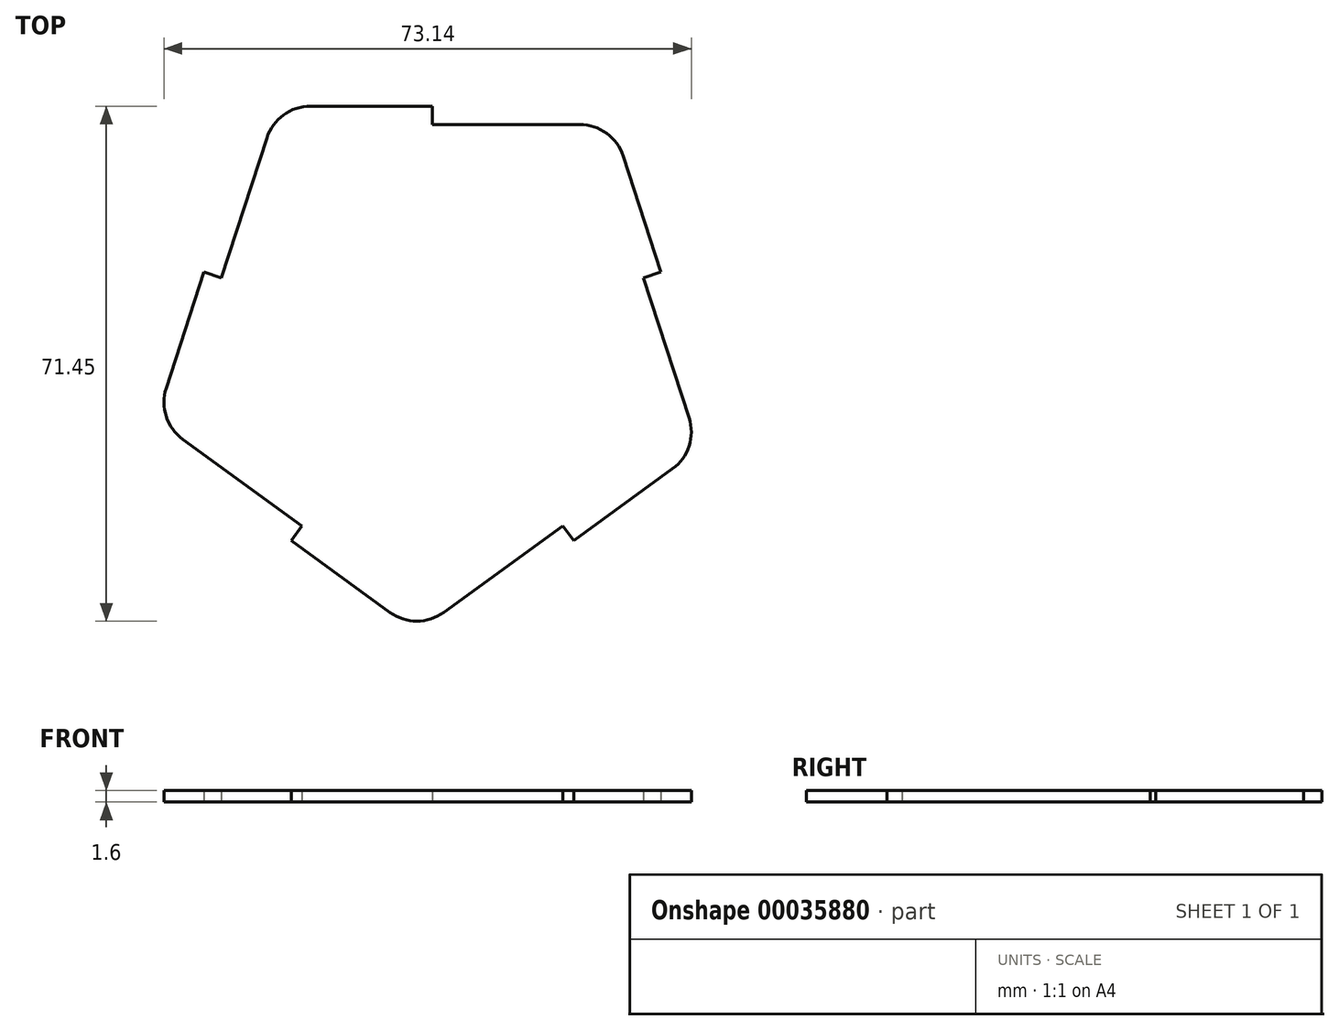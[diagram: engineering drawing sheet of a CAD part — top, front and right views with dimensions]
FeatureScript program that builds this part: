
annotation { "Feature Type Name" : "Feature", "Feature Type Description" : "" }
export const myFeature = defineFeature(function(context is Context, id is Id, definition is map)
    precondition{}
    {
        {
            var Q0;
            Q0=qCreatedBy(makeId("Top.planeOp"),FACE);
            var sketch = newSketch(context, id + "F0", { "sketchPlane" : qUnion([Q0])});
            skLineSegment(sketch, "E0", {"start": v(-24.21, 33.33) * mm, "end": v(-21.54, 33.33) * mm, "construction": true});
            skPoint(sketch, "E1", {"position": v(0, 33.33) * mm});
            skPoint(sketch, "E2.center", {"position": v(0, 0) * mm});
            skLineSegment(sketch, "E3", {"start": v(0, 33.33) * mm, "end": v(0, 30.79) * mm});
            skLineSegment(sketch, "E4", {"start": v(0, 30.79) * mm, "end": v(20.42, 30.79) * mm});
            skPoint(sketch, "E5.start.orphan", {"position": v(24.21, 33.33) * mm});
            skLineSegment(sketch, "E6", {"start": v(0, 33.33) * mm, "end": v(24.21, 33.33) * mm, "construction": true});
            skLineSegment(sketch, "E7", {"start": v(24.21, 33.33) * mm, "end": v(25.04, 30.79) * mm, "construction": true});
            skLineSegment(sketch, "E8", {"start": v(-16.93, 33.33) * mm, "end": v(0, 33.33) * mm});
            skLineSegment(sketch, "E9.1.0", {"start": v(-36.93, -5.8) * mm, "end": v(-31.7, 10.3) * mm});
            skLineSegment(sketch, "E9.1.1", {"start": v(-31.7, 10.3) * mm, "end": v(-29.28, 9.51) * mm});
            skLineSegment(sketch, "E9.1.2", {"start": v(-29.28, 9.51) * mm, "end": v(-22.97, 28.94) * mm});
            skLineSegment(sketch, "E9.2.0", {"start": v(-5.9, -36.91) * mm, "end": v(-19.59, -26.96) * mm});
            skLineSegment(sketch, "E9.2.1", {"start": v(-19.59, -26.96) * mm, "end": v(-18.1, -24.9) * mm});
            skLineSegment(sketch, "E9.2.2", {"start": v(-18.1, -24.9) * mm, "end": v(-34.62, -12.9) * mm});
            skLineSegment(sketch, "E9.3.0", {"start": v(33.28, -17.01) * mm, "end": v(19.59, -26.96) * mm});
            skLineSegment(sketch, "E9.3.1", {"start": v(19.59, -26.96) * mm, "end": v(18.1, -24.9) * mm});
            skLineSegment(sketch, "E9.3.2", {"start": v(18.1, -24.9) * mm, "end": v(1.57, -36.91) * mm});
            skLineSegment(sketch, "E9.4.0", {"start": v(26.46, 26.4) * mm, "end": v(31.7, 10.3) * mm});
            skLineSegment(sketch, "E9.4.1", {"start": v(31.7, 10.3) * mm, "end": v(29.28, 9.51) * mm});
            skLineSegment(sketch, "E9.4.2", {"start": v(29.28, 9.51) * mm, "end": v(35.6, -9.91) * mm});
            skPoint(sketch, "E10.visualSharp", {"position": v(-21.54, 33.33) * mm});
            skArc(sketch, "E10.filletArc", {"start": v(-16.93, 33.33) * mm, "mid": v(-20.66, 32.11) * mm, "end": v(-22.97, 28.94) * mm});
            skPoint(sketch, "E11.visualSharp", {"position": v(-38.35, -10.19) * mm});
            skArc(sketch, "E11.filletArc", {"start": v(-36.93, -5.8) * mm, "mid": v(-36.93, -9.73) * mm, "end": v(-34.62, -12.9) * mm});
            skPoint(sketch, "E12.visualSharp", {"position": v(-2.16, -39.62) * mm});
            skArc(sketch, "E12.filletArc", {"start": v(-5.9, -36.91) * mm, "mid": v(-2.16, -38.12) * mm, "end": v(1.57, -36.91) * mm});
            skPoint(sketch, "E13.visualSharp", {"position": v(37.02, -14.3) * mm});
            skArc(sketch, "E13.filletArc", {"start": v(33.28, -17.01) * mm, "mid": v(35.6, -13.84) * mm, "end": v(35.6, -9.91) * mm});
            skPoint(sketch, "E14.visualSharp", {"position": v(25.04, 30.79) * mm});
            skArc(sketch, "E14.filletArc", {"start": v(26.46, 26.4) * mm, "mid": v(24.16, 29.57) * mm, "end": v(20.42, 30.79) * mm});
            skSolve(sketch);
        }
        {
            var Q0;
            Q0=makeQuery(id+"F0.imprint","IMPRINT",FACE,{"disambiguationData":[TD([[makeQuery(id+"F0.imprint","IMPRINT",EDGE,{"derivedFrom":sQuery(id+"F0.wireOp",EDGE,"E3")}),-1.0]])]});
            extrude(context, id + "F1", {"entities" : qUnion([Q0]), "depth" : 1.6 * mm});
        }
        {
            var Q0;
            Q0=makeQuery(id+"F1.opExtrude","CAP_FACE",FACE,{"disambiguationData":[OSD([sQuery(id+"F0.wireOp",EDGE,"E3"),sQuery(id+"F0.wireOp",EDGE,"E4"),sQuery(id+"F0.wireOp",EDGE,"E8"),sQuery(id+"F0.wireOp",EDGE,"E9.1.0"),sQuery(id+"F0.wireOp",EDGE,"E9.1.1"),sQuery(id+"F0.wireOp",EDGE,"E9.1.2"),sQuery(id+"F0.wireOp",EDGE,"E9.2.0"),sQuery(id+"F0.wireOp",EDGE,"E9.2.1"),sQuery(id+"F0.wireOp",EDGE,"E9.2.2"),sQuery(id+"F0.wireOp",EDGE,"E9.3.0"),sQuery(id+"F0.wireOp",EDGE,"E9.3.1"),sQuery(id+"F0.wireOp",EDGE,"E9.3.2"),sQuery(id+"F0.wireOp",EDGE,"E9.4.0"),sQuery(id+"F0.wireOp",EDGE,"E9.4.1"),sQuery(id+"F0.wireOp",EDGE,"E9.4.2"),sQuery(id+"F0.wireOp",EDGE,"E10.filletArc"),sQuery(id+"F0.wireOp",EDGE,"E11.filletArc"),sQuery(id+"F0.wireOp",EDGE,"E12.filletArc"),sQuery(id+"F0.wireOp",EDGE,"E13.filletArc"),sQuery(id+"F0.wireOp",EDGE,"E14.filletArc")])],"isStart":true});
            var sketch = newSketch(context, id + "F2", { "sketchPlane" : qUnion([Q0])});
            skLineSegment(sketch, "E15", {"start": v(0, 0) * mm, "end": v(0, 22.86) * mm});
            skLineSegment(sketch, "E16.1.0", {"start": v(0, 0) * mm, "end": v(-21.74, 7.06) * mm});
            skLineSegment(sketch, "E16.2.0", {"start": v(0, 0) * mm, "end": v(-13.44, -18.5) * mm});
            skLineSegment(sketch, "E16.3.0", {"start": v(0, 0) * mm, "end": v(13.44, -18.5) * mm});
            skLineSegment(sketch, "E16.4.0", {"start": v(0, 0) * mm, "end": v(21.74, 7.06) * mm});
            skPoint(sketch, "E16.center", {"position": v(0, 0) * mm});
            skSolve(sketch);
        }
    });
